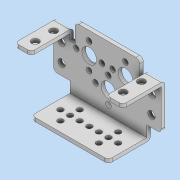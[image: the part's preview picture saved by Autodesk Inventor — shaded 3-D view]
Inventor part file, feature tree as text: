
AUTODESK INVENTOR PART (.ipt)
format: ipt  version: 2021.4 (Build 254397000, 397)  size: 225,792 bytes
history: native  units: in
note: dims shown in document units (in); Inventor stores cm internally (conversion verified against a paired STEP export)
features: extrude x2, sketch x2
ambient origin geometry x8: Origin, YZ Plane, XZ Plane, XY Plane, X Axis, Y Axis, Z Axis, Center Point
bodies: Solid2 (feature_tree), Solid1 (feature_tree)
feature tree (4):
  extrude  "Extrusion1"  Depth=0.0787in TaperAngle=0.0deg
  extrude  "Extrusion2"  Depth=0.1181in
  sketch  "Sketch1"  dims[d0=0.0709in d1=0.0787in d2=0.0in]
  sketch  "Sketch2"  dims[d3=0.1181in d4=0.1181in d5=0.1575in d6=0.1575in d7=0.5906in d8=0.0787in d9=0.0in]
